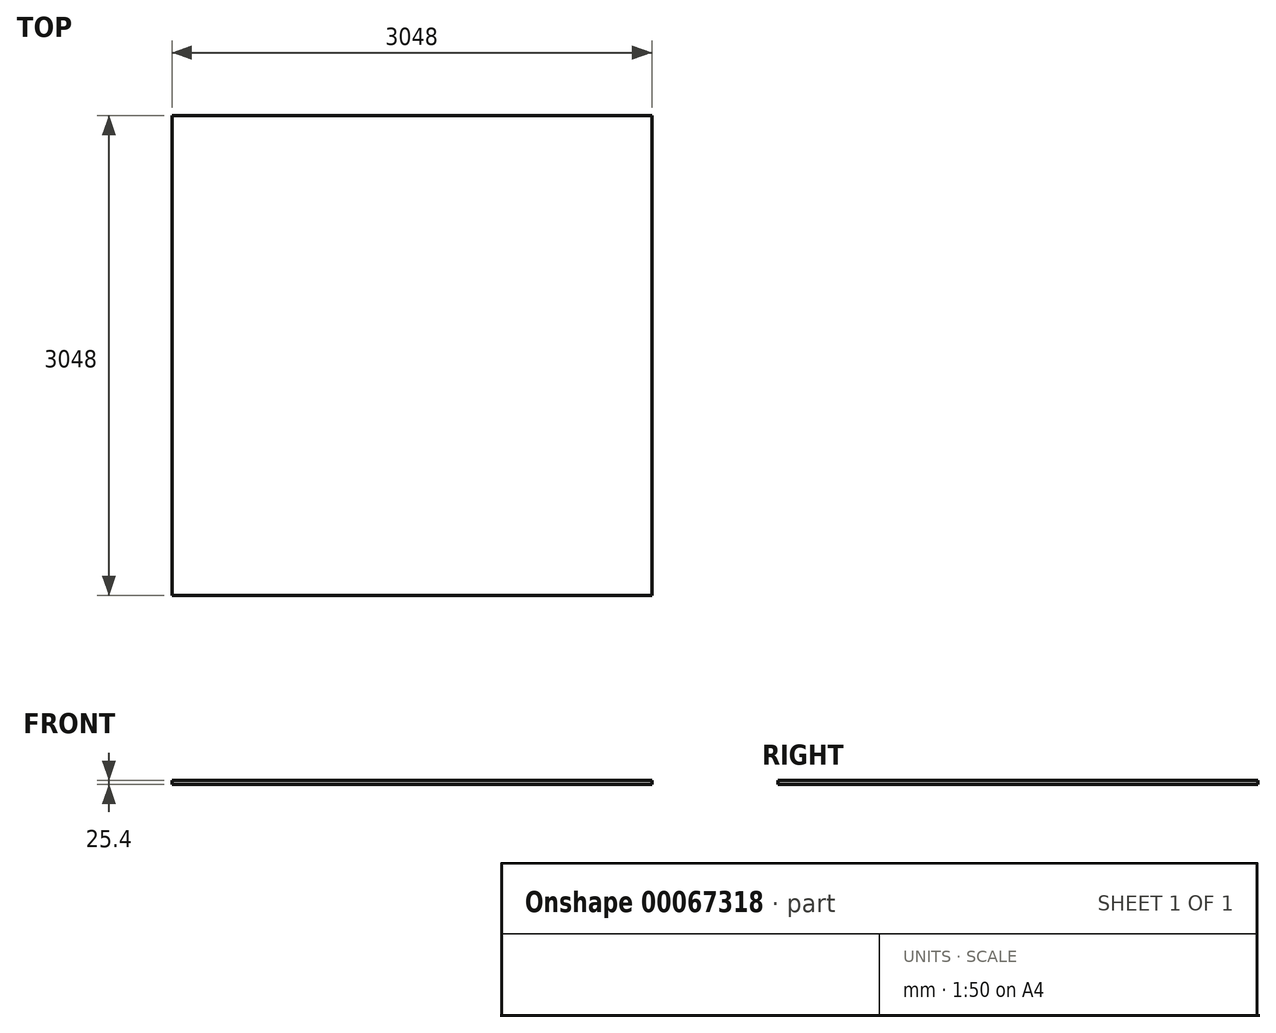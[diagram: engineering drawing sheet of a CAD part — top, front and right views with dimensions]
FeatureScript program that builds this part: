
annotation { "Feature Type Name" : "Feature", "Feature Type Description" : "" }
export const myFeature = defineFeature(function(context is Context, id is Id, definition is map)
    precondition{}
    {
        {
            var Q0;
            Q0=qCreatedBy(makeId("Top.planeOp"),FACE);
            var sketch = newSketch(context, id + "F0", { "sketchPlane" : qUnion([Q0])});
            skLineSegment(sketch, "E0.bottom", {"start": v(-1518.51, 1425.6) * mm, "end": v(1529.49, 1425.6) * mm});
            skLineSegment(sketch, "E0.top", {"start": v(-1518.51, -1622.4) * mm, "end": v(1529.49, -1622.4) * mm});
            skLineSegment(sketch, "E0.left", {"start": v(-1518.51, 1425.6) * mm, "end": v(-1518.51, -1622.4) * mm});
            skLineSegment(sketch, "E0.right", {"start": v(1529.49, 1425.6) * mm, "end": v(1529.49, -1622.4) * mm});
            skSolve(sketch);
        }
        {
            var Q0;
            Q0=makeQuery(id+"F0.imprint","IMPRINT",FACE,{"disambiguationData":[TD([[makeQuery(id+"F0.imprint","IMPRINT",EDGE,{"derivedFrom":sQuery(id+"F0.wireOp",EDGE,"E0.bottom")}),-1.0]])]});
            extrude(context, id + "F1", {"entities" : qUnion([Q0]), "depth" : 25.4 * mm});
        }
    });
